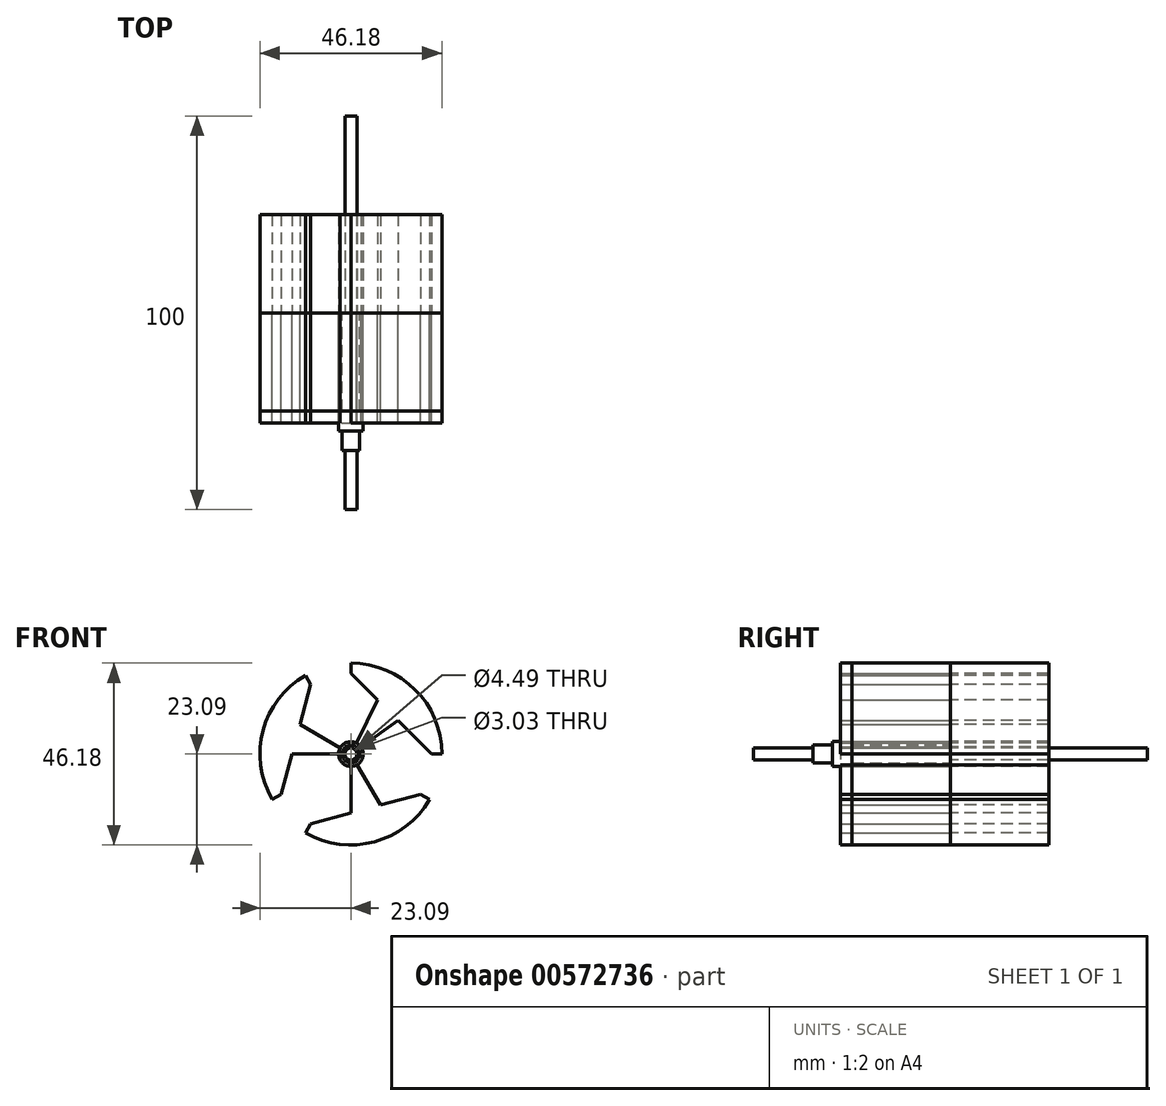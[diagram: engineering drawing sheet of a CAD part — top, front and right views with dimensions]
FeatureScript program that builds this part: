
annotation { "Feature Type Name" : "Feature", "Feature Type Description" : "" }
export const myFeature = defineFeature(function(context is Context, id is Id, definition is map)
    precondition{}
    {
        {
            var Q0;
            Q0=qCreatedBy(makeId("Front.planeOp"),FACE);
            var sketch = newSketch(context, id + "F0", { "sketchPlane" : qUnion([Q0])});
            skCircle(sketch, "E0", {"center": v(0, 0) * mm, "radius": 1.52 * mm});
            skCircle(sketch, "E1", {"center": v(0, 0) * mm, "radius": 2.24 * mm});
            skCircle(sketch, "E2", {"center": v(0, 0) * mm, "radius": 3.14 * mm});
            skArc(sketch, "E3", {"start": v(-11.55, 20) * mm, "mid": v(-22.3, 5.98) * mm, "end": v(-20, -11.55) * mm});
            skLineSegment(sketch, "E4", {"start": v(-10.23, 17.72) * mm, "end": v(-12.97, 7.49) * mm});
            skLineSegment(sketch, "E5", {"start": v(-10.23, -17.72) * mm, "end": v(0, -14.98) * mm});
            skArc(sketch, "E6.trimOffspring", {"start": v(23.1, 0) * mm, "mid": v(16.33, 16.33) * mm, "end": v(0, 23.1) * mm});
            skArc(sketch, "E7.trimOffspring", {"start": v(-11.55, -20) * mm, "mid": v(5.98, -22.3) * mm, "end": v(20, -11.55) * mm});
            skLineSegment(sketch, "E8", {"start": v(2.56, 1.81) * mm, "end": v(11.99, 8.47) * mm});
            skLineSegment(sketch, "E9", {"start": v(0, 20.45) * mm, "end": v(6.75, 13.7) * mm});
            skLineSegment(sketch, "E10.trimOffspring", {"start": v(0, 20.45) * mm, "end": v(0, 23.1) * mm});
            skLineSegment(sketch, "E11.trimOffspring", {"start": v(20.46, 0) * mm, "end": v(23.1, 0) * mm});
            skLineSegment(sketch, "E12.trimOffspring", {"start": v(11.99, 8.47) * mm, "end": v(20.46, 0) * mm});
            skPoint(sketch, "E13.endSnap0", {"position": v(5.98, -22.3) * mm});
            skLineSegment(sketch, "E14", {"start": v(1.57, -2.72) * mm, "end": v(7.49, -12.97) * mm});
            skLineSegment(sketch, "E15.trimOffspring", {"start": v(7.49, -12.97) * mm, "end": v(17.72, -10.23) * mm});
            skLineSegment(sketch, "E16.trimOffspring", {"start": v(17.72, -10.23) * mm, "end": v(20, -11.55) * mm});
            skLineSegment(sketch, "E17.trimOffspring", {"start": v(-10.23, -17.72) * mm, "end": v(-11.55, -20) * mm});
            skLineSegment(sketch, "E18.trimOffspring", {"start": v(-14.98, 0) * mm, "end": v(-17.72, -10.23) * mm});
            skLineSegment(sketch, "E19.trimOffspring", {"start": v(-17.72, -10.23) * mm, "end": v(-20, -11.55) * mm});
            skLineSegment(sketch, "E20.trimOffspring", {"start": v(-10.23, 17.72) * mm, "end": v(-11.55, 20) * mm});
            skLineSegment(sketch, "E21.trimOffspring", {"start": v(-2.72, 1.57) * mm, "end": v(-12.97, 7.49) * mm});
            skLineSegment(sketch, "E22.trimOffspring", {"start": v(-3.14, 0) * mm, "end": v(-14.98, 0) * mm});
            skLineSegment(sketch, "E23.trimOffspring", {"start": v(0, -3.14) * mm, "end": v(0, -14.98) * mm});
            skLineSegment(sketch, "E24.trimOffspring", {"start": v(1.39, 2.82) * mm, "end": v(6.75, 13.7) * mm});
            skSolve(sketch);
        }
        {
            var Q0;
            Q0=makeQuery(id+"F0.imprint","IMPRINT",FACE,{"disambiguationData":[TD([[makeQuery(id+"F0.imprint","IMPRINT",EDGE,{"derivedFrom":sQuery(id+"F0.wireOp",EDGE,"E3")}),1.0]])]});
            var Q1;
            Q1=makeQuery(id+"F0.imprint","IMPRINT",FACE,{"disambiguationData":[TD([[makeQuery(id+"F0.imprint","IMPRINT",EDGE,{"derivedFrom":sQuery(id+"F0.wireOp",EDGE,"E6.trimOffspring")}),1.0]])]});
            var Q2;
            Q2=makeQuery(id+"F0.imprint","IMPRINT",FACE,{"disambiguationData":[TD([[makeQuery(id+"F0.imprint","IMPRINT",EDGE,{"derivedFrom":sQuery(id+"F0.wireOp",EDGE,"E5")}),-1.0]])]});
            extrude(context, id + "F1", {"entities" : qUnion([Q0, Q1, Q2]), "depth" : 28 * mm, "offsetDistance" : 25 * mm});
        }
        {
            var Q0;
            Q0=makeQuery(id+"F0.imprint","IMPRINT",FACE,{"disambiguationData":[TD([[makeQuery(id+"F0.imprint","IMPRINT",EDGE,{"derivedFrom":sQuery(id+"F0.wireOp",EDGE,"E1")}),-1.0]])]});
            extrude(context, id + "F2", {"entities" : qUnion([Q0]), "depth" : 30 * mm, "offsetDistance" : 25 * mm});
        }
        {
            var Q0;
            Q0=makeQuery(id+"F0.imprint","IMPRINT",FACE,{"disambiguationData":[TD([[makeQuery(id+"F0.imprint","IMPRINT",EDGE,{"derivedFrom":sQuery(id+"F0.wireOp",EDGE,"E0")}),-1.0]])]});
            extrude(context, id + "F3", {"entities" : qUnion([Q0]), "operationType" : NewBodyOperationType.ADD, "depth" : 35 * mm, "offsetDistance" : 25 * mm});
        }
        {
            var Q0;
            Q0=makeQuery(id+"F0.imprint","IMPRINT",FACE,{"disambiguationData":[TD([[makeQuery(id+"F0.imprint","IMPRINT",EDGE,{"derivedFrom":sQuery(id+"F0.wireOp",EDGE,"E0")}),1.0]])]});
            extrude(context, id + "F4", {"entities" : qUnion([Q0]), "operationType" : NewBodyOperationType.ADD, "depth" : 50 * mm, "offsetDistance" : 25 * mm});
        }
        {
            var Q0;
            Q0=makeQuery(id+"F0.imprint","IMPRINT",FACE,{"disambiguationData":[TD([[makeQuery(id+"F0.imprint","IMPRINT",EDGE,{"derivedFrom":sQuery(id+"F0.wireOp",EDGE,"E0")}),1.0]])]});
            extrude(context, id + "F5", {"entities" : qUnion([Q0]), "operationType" : NewBodyOperationType.ADD, "oppositeDirection" : true, "depth" : 50 * mm, "offsetDistance" : 25 * mm});
        }
        {
            var Q0;
            Q0=makeQuery(id+"F0.imprint","IMPRINT",FACE,{"disambiguationData":[TD([[makeQuery(id+"F0.imprint","IMPRINT",EDGE,{"derivedFrom":sQuery(id+"F0.wireOp",EDGE,"E6.trimOffspring")}),1.0]])]});
            var Q1;
            Q1=makeQuery(id+"F0.imprint","IMPRINT",FACE,{"disambiguationData":[TD([[makeQuery(id+"F0.imprint","IMPRINT",EDGE,{"derivedFrom":sQuery(id+"F0.wireOp",EDGE,"E3")}),1.0]])]});
            var Q2;
            Q2=makeQuery(id+"F0.imprint","IMPRINT",FACE,{"disambiguationData":[TD([[makeQuery(id+"F0.imprint","IMPRINT",EDGE,{"derivedFrom":sQuery(id+"F0.wireOp",EDGE,"E5")}),-1.0]])]});
            var Q3;
            Q3=makeQuery(id+"F0.imprint","IMPRINT",FACE,{"disambiguationData":[TD([[makeQuery(id+"F0.imprint","IMPRINT",EDGE,{"derivedFrom":sQuery(id+"F0.wireOp",EDGE,"E1")}),-1.0]])]});
            var Q4;
            Q4=makeQuery(id+"F0.imprint","IMPRINT",FACE,{"disambiguationData":[TD([[makeQuery(id+"F0.imprint","IMPRINT",EDGE,{"derivedFrom":sQuery(id+"F0.wireOp",EDGE,"E0")}),-1.0]])]});
            extrude(context, id + "F6", {"entities" : qUnion([Q0, Q1, Q2, Q3, Q4]), "oppositeDirection" : true, "depth" : 25 * mm, "offsetDistance" : 25 * mm});
        }
        {
            var Q0;
            Q0 = qSketchRegion(id + "F0", true);
            extrude(context, id + "F7", {"entities" : qUnion([Q0]), "depth" : 25 * mm, "offsetDistance" : 25 * mm});
        }
    });
